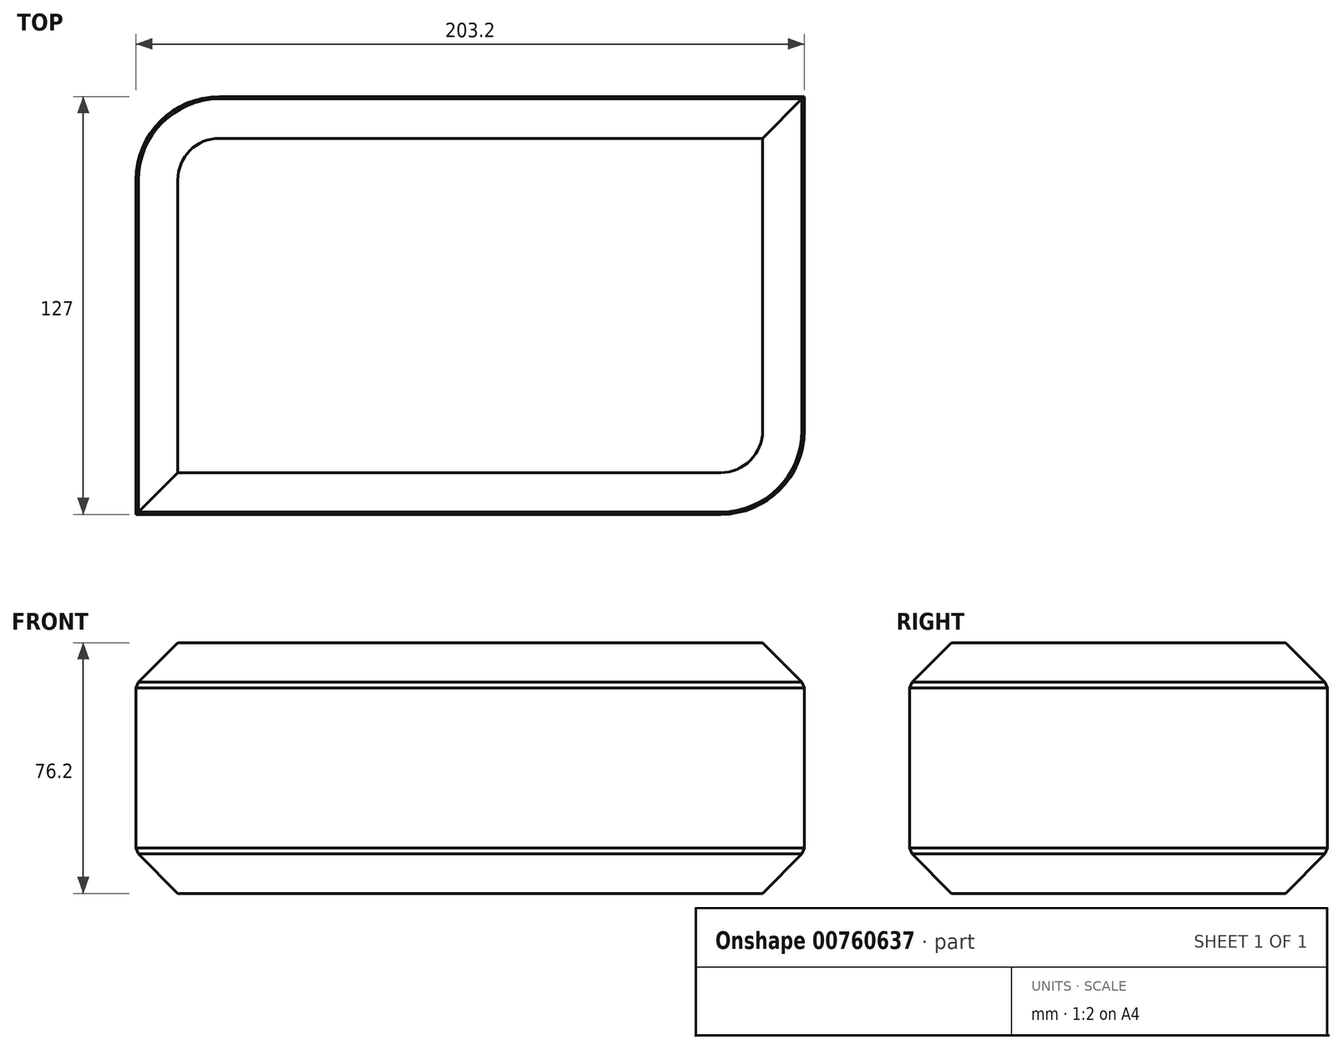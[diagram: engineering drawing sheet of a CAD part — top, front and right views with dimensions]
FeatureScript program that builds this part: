
annotation { "Feature Type Name" : "Feature", "Feature Type Description" : "" }
export const myFeature = defineFeature(function(context is Context, id is Id, definition is map)
    precondition{}
    {
        {
            var Q0;
            Q0=qCreatedBy(makeId("Top.planeOp"),FACE);
            var sketch = newSketch(context, id + "F0", { "sketchPlane" : qUnion([Q0])});
            skLineSegment(sketch, "E0.bottom", {"start": v(-40.79, 56.48) * mm, "end": v(137.01, 56.48) * mm});
            skLineSegment(sketch, "E0.top", {"start": v(-66.19, -70.52) * mm, "end": v(111.61, -70.52) * mm});
            skLineSegment(sketch, "E0.left", {"start": v(-66.19, 31.08) * mm, "end": v(-66.19, -70.52) * mm});
            skLineSegment(sketch, "E0.right", {"start": v(137.01, 56.48) * mm, "end": v(137.01, -45.12) * mm});
            skPoint(sketch, "E1.visualSharp", {"position": v(137.01, -70.52) * mm});
            skArc(sketch, "E1.filletArc", {"start": v(111.61, -70.52) * mm, "mid": v(129.57, -63.09) * mm, "end": v(137.01, -45.12) * mm});
            skPoint(sketch, "E2.visualSharp", {"position": v(-66.19, 56.48) * mm});
            skArc(sketch, "E2.filletArc", {"start": v(-40.79, 56.48) * mm, "mid": v(-58.75, 49.04) * mm, "end": v(-66.19, 31.08) * mm});
            skSolve(sketch);
        }
        {
            var Q0;
            Q0 = qSketchRegion(id + "F0", true);
            extrude(context, id + "F1", {"entities" : qUnion([Q0]), "depth" : 76.2 * mm, "offsetDistance" : 25.4 * mm});
        }
        {
            var Q0;
            Q0=makeQuery(id+"F1.opExtrude","CAP_FACE",FACE,{"disambiguationData":[OSD([sQuery(id+"F0.wireOp",EDGE,"E0.bottom"),sQuery(id+"F0.wireOp",EDGE,"E0.top"),sQuery(id+"F0.wireOp",EDGE,"E0.left"),sQuery(id+"F0.wireOp",EDGE,"E0.right"),sQuery(id+"F0.wireOp",EDGE,"E1.filletArc"),sQuery(id+"F0.wireOp",EDGE,"E2.filletArc")])],"isStart":false});
            var Q1;
            Q1=makeQuery(id+"F1.opExtrude","CAP_FACE",FACE,{"disambiguationData":[OSD([sQuery(id+"F0.wireOp",EDGE,"E0.bottom"),sQuery(id+"F0.wireOp",EDGE,"E0.top"),sQuery(id+"F0.wireOp",EDGE,"E0.left"),sQuery(id+"F0.wireOp",EDGE,"E0.right"),sQuery(id+"F0.wireOp",EDGE,"E1.filletArc"),sQuery(id+"F0.wireOp",EDGE,"E2.filletArc")])],"isStart":true});
            chamfer(context, id + "F2", {"entities" : qUnion([Q0, Q1]), "width" : 12.7 * mm, "tangentPropagation" : true});
        }
        {
            var Q0;
            Q0=makeQuery(id+"F1.opExtrude","SWEPT_FACE",FACE,{"disambiguationData":[OSD([sQuery(id+"F0.wireOp",EDGE,"E1.filletArc")])]});
            var Q1;
            Q1=makeQuery(id+"F1.opExtrude","SWEPT_FACE",FACE,{"disambiguationData":[OSD([sQuery(id+"F0.wireOp",EDGE,"E2.filletArc")])]});
            chamfer(context, id + "F3", {"entities" : qUnion([Q0, Q1]), "width" : 2.54 * mm, "tangentPropagation" : true});
        }
    });
